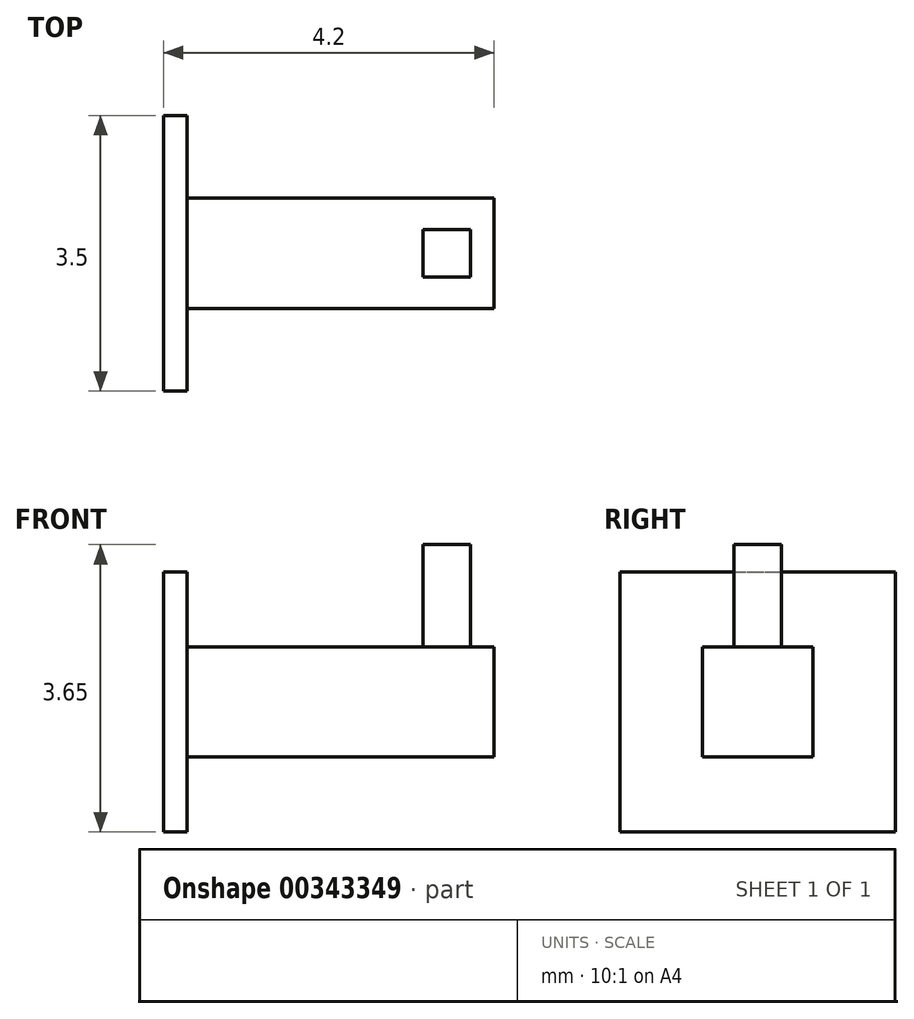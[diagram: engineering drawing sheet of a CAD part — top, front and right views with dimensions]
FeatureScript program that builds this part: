
annotation { "Feature Type Name" : "Feature", "Feature Type Description" : "" }
export const myFeature = defineFeature(function(context is Context, id is Id, definition is map)
    precondition{}
    {
        {
            var Q0;
            Q0=qCreatedBy(makeId("Front.planeOp"),FACE);
            var sketch = newSketch(context, id + "F0", { "sketchPlane" : qUnion([Q0])});
            skLineSegment(sketch, "E0.bottom", {"start": v(1.95, 0.7) * mm, "end": v(-1.95, 0.7) * mm});
            skLineSegment(sketch, "E0.top", {"start": v(1.95, -0.7) * mm, "end": v(-1.95, -0.7) * mm});
            skLineSegment(sketch, "E0.left", {"start": v(1.95, 0.7) * mm, "end": v(1.95, -0.7) * mm});
            skLineSegment(sketch, "E0.right", {"start": v(-1.95, 0.7) * mm, "end": v(-1.95, -0.7) * mm});
            skPoint(sketch, "E0.middle", {"position": v(0, 0) * mm});
            skLineSegment(sketch, "E1", {"start": v(1.65, 0.7) * mm, "end": v(1.65, 2) * mm});
            skLineSegment(sketch, "E2", {"start": v(1.65, 2) * mm, "end": v(1.05, 2) * mm});
            skLineSegment(sketch, "E3", {"start": v(1.05, 2) * mm, "end": v(1.05, 0.7) * mm});
            skLineSegment(sketch, "E4", {"start": v(-1.95, 0.7) * mm, "end": v(-1.95, 1.65) * mm});
            skLineSegment(sketch, "E5", {"start": v(-1.95, -0.7) * mm, "end": v(-1.95, -1.65) * mm});
            skLineSegment(sketch, "E6", {"start": v(-1.95, -1.65) * mm, "end": v(-2.25, -1.65) * mm});
            skLineSegment(sketch, "E7", {"start": v(-2.25, -1.65) * mm, "end": v(-2.25, 1.65) * mm});
            skLineSegment(sketch, "E8", {"start": v(-2.25, 1.65) * mm, "end": v(-1.95, 1.65) * mm});
            skSolve(sketch);
        }
        {
            var Q0;
            Q0=makeQuery(id+"F0.imprint","IMPRINT",FACE,{"disambiguationData":[TD([[makeQuery(id+"F0.imprint","IMPRINT",EDGE,{"derivedFrom":sQuery(id+"F0.wireOp",EDGE,"E0.right")}),-1.0]])]});
            extrude(context, id + "F1", {"entities" : qUnion([Q0]), "endBound" : BoundingType.SYMMETRIC, "depth" : 3.5 * mm});
        }
        {
            var Q0;
            Q0=makeQuery(id+"F0.imprint","IMPRINT",FACE,{"disambiguationData":[TD([[makeQuery(id+"F0.imprint","IMPRINT",EDGE,{"derivedFrom":sQuery(id+"F0.wireOp",EDGE,"E0.top")}),-1.0]])]});
            extrude(context, id + "F2", {"entities" : qUnion([Q0]), "operationType" : NewBodyOperationType.ADD, "endBound" : BoundingType.SYMMETRIC, "depth" : 1.4 * mm});
        }
        {
            var Q0;
            {var subQ0=sQuery(id+"F0.wireOp",EDGE,"E1");Q0=makeQuery(id+"F0.imprint","IMPRINT",FACE,{"disambiguationData":[TD([[makeQuery(id+"F0.imprint","IMPRINT",EDGE,{"derivedFrom":subQ0}),1.0]])]});}
            extrude(context, id + "F3", {"entities" : qUnion([Q0]), "operationType" : NewBodyOperationType.ADD, "endBound" : BoundingType.SYMMETRIC, "depth" : 0.6 * mm});
        }
    });
